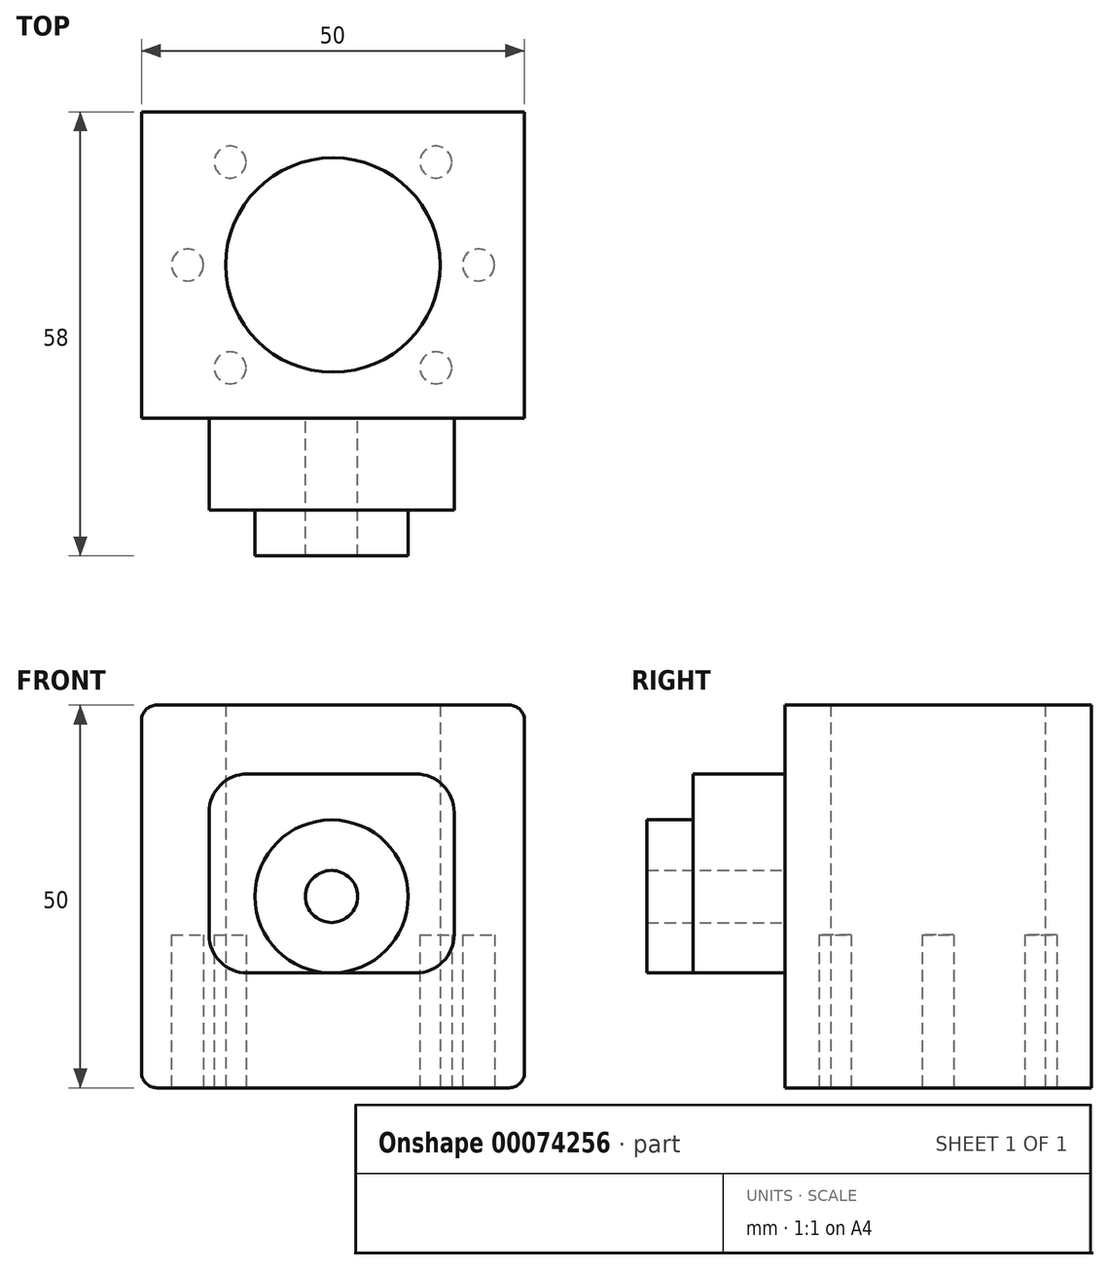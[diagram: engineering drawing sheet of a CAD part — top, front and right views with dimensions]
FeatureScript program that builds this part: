
annotation { "Feature Type Name" : "Feature", "Feature Type Description" : "" }
export const myFeature = defineFeature(function(context is Context, id is Id, definition is map)
    precondition{}
    {
        {
            var Q0;
            Q0=qCreatedBy(makeId("Front.planeOp"),FACE);
            var sketch = newSketch(context, id + "F0", { "sketchPlane" : qUnion([Q0])});
            skLineSegment(sketch, "E0.bottom", {"start": v(17.72, -4.73) * mm, "end": v(63.72, -4.73) * mm});
            skLineSegment(sketch, "E0.top", {"start": v(17.72, -54.73) * mm, "end": v(63.72, -54.73) * mm});
            skLineSegment(sketch, "E0.left", {"start": v(15.72, -6.73) * mm, "end": v(15.72, -52.73) * mm});
            skLineSegment(sketch, "E0.right", {"start": v(65.72, -6.73) * mm, "end": v(65.72, -52.73) * mm});
            skPoint(sketch, "E1.visualSharp", {"position": v(15.72, -4.73) * mm});
            skArc(sketch, "E1.filletArc", {"start": v(17.72, -4.73) * mm, "mid": v(16.3, -5.32) * mm, "end": v(15.72, -6.73) * mm});
            skPoint(sketch, "E2.visualSharp", {"position": v(65.72, -4.73) * mm});
            skArc(sketch, "E2.filletArc", {"start": v(65.72, -6.73) * mm, "mid": v(65.13, -5.32) * mm, "end": v(63.72, -4.73) * mm});
            skPoint(sketch, "E3.visualSharp", {"position": v(65.72, -54.73) * mm});
            skArc(sketch, "E3.filletArc", {"start": v(63.72, -54.73) * mm, "mid": v(65.13, -54.15) * mm, "end": v(65.72, -52.73) * mm});
            skPoint(sketch, "E4.visualSharp", {"position": v(15.72, -54.73) * mm});
            skArc(sketch, "E4.filletArc", {"start": v(15.72, -52.73) * mm, "mid": v(16.3, -54.15) * mm, "end": v(17.72, -54.73) * mm});
            skSolve(sketch);
        }
        {
            var Q0;
            Q0=makeQuery(id+"F0.imprint","IMPRINT",FACE,{"disambiguationData":[TD([[makeQuery(id+"F0.imprint","IMPRINT",EDGE,{"derivedFrom":sQuery(id+"F0.wireOp",EDGE,"E0.bottom")}),-1.0]])]});
            var sketch = newSketch(context, id + "F1", { "sketchPlane" : qUnion([Q0])});
            skLineSegment(sketch, "E5.bottom", {"start": v(29.53, -13.73) * mm, "end": v(51.53, -13.73) * mm});
            skLineSegment(sketch, "E5.top", {"start": v(29.53, -39.73) * mm, "end": v(51.53, -39.73) * mm});
            skLineSegment(sketch, "E5.left", {"start": v(24.53, -18.73) * mm, "end": v(24.53, -34.73) * mm});
            skLineSegment(sketch, "E5.right", {"start": v(56.53, -18.73) * mm, "end": v(56.53, -34.73) * mm});
            skPoint(sketch, "E6.visualSharp", {"position": v(24.53, -13.73) * mm});
            skArc(sketch, "E6.filletArc", {"start": v(29.53, -13.73) * mm, "mid": v(26, -15.2) * mm, "end": v(24.53, -18.73) * mm});
            skPoint(sketch, "E7.visualSharp", {"position": v(56.53, -13.73) * mm});
            skArc(sketch, "E7.filletArc", {"start": v(56.53, -18.73) * mm, "mid": v(55.07, -15.2) * mm, "end": v(51.53, -13.73) * mm});
            skPoint(sketch, "E8.visualSharp", {"position": v(56.53, -39.73) * mm});
            skArc(sketch, "E8.filletArc", {"start": v(51.53, -39.73) * mm, "mid": v(55.07, -38.27) * mm, "end": v(56.53, -34.73) * mm});
            skPoint(sketch, "E9.visualSharp", {"position": v(24.53, -39.73) * mm});
            skArc(sketch, "E9.filletArc", {"start": v(24.53, -34.73) * mm, "mid": v(26, -38.27) * mm, "end": v(29.53, -39.73) * mm});
            skSolve(sketch);
        }
        {
            var Q0;
            Q0=makeQuery(id+"F0.imprint","IMPRINT",FACE,{"disambiguationData":[TD([[makeQuery(id+"F0.imprint","IMPRINT",EDGE,{"derivedFrom":sQuery(id+"F0.wireOp",EDGE,"E0.bottom")}),-1.0]])]});
            var sketch = newSketch(context, id + "F2", { "sketchPlane" : qUnion([Q0])});
            skCircle(sketch, "E10", {"center": v(40.53, -29.73) * mm, "radius": 10 * mm});
            skSolve(sketch);
        }
        {
            var Q0;
            Q0=makeQuery(id+"F0.imprint","IMPRINT",FACE,{"disambiguationData":[TD([[makeQuery(id+"F0.imprint","IMPRINT",EDGE,{"derivedFrom":sQuery(id+"F0.wireOp",EDGE,"E0.bottom")}),-1.0]])]});
            var sketch = newSketch(context, id + "F3", { "sketchPlane" : qUnion([Q0])});
            skCircle(sketch, "E11", {"center": v(40.53, -29.73) * mm, "radius": 3.4 * mm});
            skSolve(sketch);
        }
        {
            var Q0;
            Q0 = qSketchRegion(id + "F1", true);
            extrude(context, id + "F4", {"entities" : qUnion([Q0]), "depth" : 12 * mm});
        }
        {
            var Q0;
            Q0 = qSketchRegion(id + "F2", true);
            extrude(context, id + "F5", {"entities" : qUnion([Q0]), "operationType" : NewBodyOperationType.ADD, "depth" : 6 * mm});
        }
        {
            var Q0;
            Q0 = qSketchRegion(id + "F3", true);
            extrude(context, id + "F6", {"entities" : qUnion([Q0]), "operationType" : NewBodyOperationType.REMOVE, "endBound" : BoundingType.THROUGH_ALL, "depth" : 25 * mm});
        }
        {
            var Q0;
            Q0 = qSketchRegion(id + "F0", true);
            extrude(context, id + "F7", {"entities" : qUnion([Q0]), "operationType" : NewBodyOperationType.ADD, "oppositeDirection" : true, "depth" : 40 * mm});
        }
        {
            var Q0;
            Q0=makeQuery(id+"F7.opExtrude","SWEPT_FACE",FACE,{"disambiguationData":[OSD([sQuery(id+"F0.wireOp",EDGE,"E0.top")])]});
            var sketch = newSketch(context, id + "F8", { "sketchPlane" : qUnion([Q0])});
            skCircle(sketch, "E12", {"center": v(40.72, -20) * mm, "radius": 14 * mm});
            skSolve(sketch);
        }
        {
            var Q0;
            Q0=makeQuery(id+"F8.imprint","IMPRINT",FACE,{"disambiguationData":[TD([[makeQuery(id+"F8.imprint","IMPRINT",EDGE,{"derivedFrom":sQuery(id+"F8.wireOp",EDGE,"E12")}),-1.0]])]});
            var sketch = newSketch(context, id + "F9", { "sketchPlane" : qUnion([Q0])});
            skCircle(sketch, "E13", {"center": v(27.28, -6.56) * mm, "radius": 2.09 * mm});
            skCircle(sketch, "E14.1.0", {"center": v(21.72, -20) * mm, "radius": 2.09 * mm});
            skCircle(sketch, "E14.2.0", {"center": v(27.28, -33.44) * mm, "radius": 2.09 * mm});
            skPoint(sketch, "E14.center", {"position": v(40.72, -20) * mm});
            skCircle(sketch, "E15.MirrorC", {"center": v(54.15, -6.56) * mm, "radius": 2.09 * mm});
            skCircle(sketch, "E16.MirrorC", {"center": v(59.72, -20) * mm, "radius": 2.09 * mm});
            skCircle(sketch, "E17.MirrorC", {"center": v(54.15, -33.44) * mm, "radius": 2.09 * mm});
            skSolve(sketch);
        }
        {
            var Q0;
            Q0=makeQuery(id+"F9.imprint","IMPRINT",FACE,{"disambiguationData":[TD([[makeQuery(id+"F9.imprint","IMPRINT",EDGE,{"derivedFrom":makeQuery(id+"F8.imprint","IMPRINT",EDGE,{"derivedFrom":sQuery(id+"F8.wireOp",EDGE,"E12")})}),1.0]])]});
            extrude(context, id + "F10", {"entities" : qUnion([Q0]), "operationType" : NewBodyOperationType.REMOVE, "endBound" : BoundingType.THROUGH_ALL, "oppositeDirection" : true, "depth" : 25 * mm});
        }
        {
            var Q0;
            Q0 = qSketchRegion(id + "F9", true);
            extrude(context, id + "F11", {"entities" : qUnion([Q0]), "operationType" : NewBodyOperationType.REMOVE, "oppositeDirection" : true, "depth" : 20 * mm});
        }
        {
            var Q0;
            Q0=makeQuery(id+"F4.opExtrude","CAP_FACE",FACE,{"disambiguationData":[OSD([sQuery(id+"F1.wireOp",EDGE,"E5.bottom"),sQuery(id+"F1.wireOp",EDGE,"E5.top"),sQuery(id+"F1.wireOp",EDGE,"E5.left"),sQuery(id+"F1.wireOp",EDGE,"E5.right"),sQuery(id+"F1.wireOp",EDGE,"E6.filletArc"),sQuery(id+"F1.wireOp",EDGE,"E7.filletArc"),sQuery(id+"F1.wireOp",EDGE,"E8.filletArc"),sQuery(id+"F1.wireOp",EDGE,"E9.filletArc")])],"isStart":false});
            var sketch = newSketch(context, id + "F12", { "sketchPlane" : qUnion([Q0])});
            skCircle(sketch, "E18", {"center": v(40.53, -29.73) * mm, "radius": 10 * mm});
            skSolve(sketch);
        }
        {
            var Q0;
            Q0 = qSketchRegion(id + "F12", true);
            extrude(context, id + "F13", {"entities" : qUnion([Q0]), "operationType" : NewBodyOperationType.ADD, "depth" : 6 * mm});
        }
        {
            var Q0;
            Q0 = qSketchRegion(id + "F3", true);
            extrude(context, id + "F14", {"entities" : qUnion([Q0]), "operationType" : NewBodyOperationType.REMOVE, "depth" : 25 * mm});
        }
    });
